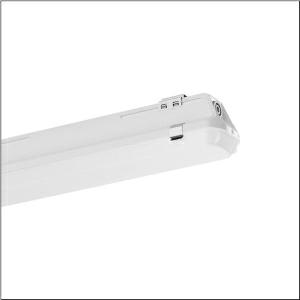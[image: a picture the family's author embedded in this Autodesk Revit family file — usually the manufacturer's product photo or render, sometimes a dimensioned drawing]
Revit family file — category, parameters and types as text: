
# Revit family: monsun_r__21_51fb10dl420j_0d51
name_source: partatom
category: Lighting Fixtures
units: mm (PartAtom-declared; Revit-internal decimal feet)

## family parameters
Cut with Voids When Loaded = No
Host = Face
Light Source = No
Part Type = Normal
Room Calculation Point = No
Round Connector Dimension = Use Diameter
Shared = No

## types (1)
- --- (1 x LED, 2630 lm, 16.6 W, 4000K)
    Apparent Load = 17 VA
    CIE Flux Codes = 46 76 93 94 100
    Color Rendering = 80
    Color Temperature = 4000K
    Default Elevation = 1800 mm
    Description = Monsun® 21, damp-proof luminaire, chain hanger, primary optical cover: enclosure, of PMMA, light emission: direct distribution, primary light characteristic: symmetric, installation type: suspended mounting, surface-mounted, horizontal mounting, vertical mounting, LED, rated luminous flux: 2.660lm, luminous efficacy: 155lm/W, light colour: 840, colour temperature: 4000K, control gear: ECG DALI, with terminal, 5-pole, max. 2.5mm², mains connection: 220..240V, AC, 50/60Hz, rated input power: 17W, housing, of glass-fibre reinforced plastic, uncoated, bright grey, incl. chain hanger, length: 1.299mm, width: 90mm, height: 88mm, clip for enclosure, of stainless steel (V2A), ceiling mounting element, of stainless steel (V2A), chain hanger, of stainless steel (V2A), protection rating (complete): IP66, insulation class (complete): insulation class I (protective earthing), certification: CE, ENEC, VDE, UKCA, protection symbol: D, impact resistance: IK04, permissible operating ambient temperature: -25..+35°C, standard: EN 50419, EN 60598-2-1, corresponds to IFS (International Featured Standards) requirements for safety and quality in the food industry, for indoor or canopied outdoor use, no direct snow, no direct sun, no direct rain, contact your sales advisor before using the luminaires in applications with unclear chemical exposure, large temperature fluctuations or condensation-forming humidity, LABS conformity tested according to VDMA 24364:2018-05, packaging unit: 1 piece
    Height = 88 mm
    Lamp = 1 x LED
    Lamp Light Flux = 2630 lm
    Lamp Power = 16.6 W
    Lamp count = 1
    Length = 1299 mm
    Luminous efficacy = 158 lm/W
    Manufacturer = Siteco
    ModVariant = No
    Model = 51FB10DL420J
    Mounting Place = Ceiling
    Mounting Type = Surface mounted
    Number of Poles = 1
    OnlyDefault = Yes
    Power Factor = 1
    Product Name = Monsun® 21
    Product group = damp-proof luminaire
    ProductGroupID = 300
    Protection Class = Protection class I
    Protection Degree = IP 66
    RLX_Detail_Level = 1
    RLX_Emergency_Light_Flux = 0 lm
    RLX_Emergency_Type = 0
    RLX_Emergency_Type_DB = No
    RlxData = <blob elided: 93601 chars, md5=ac2ac200>
    Socket = socket
    Standby Power = 0 W
    System Light Flux = 2630 lm
    System Power = 17 W
    Type Comments = factory setting: luminous flux: 100 % | dim-lin: 254 | 107 mA
    Type Image = l_1006717.jpg
    URL = http://relux.com
    VarID = @adj_078033
    Voltage = 0 V
    Weight = 0.00 kg
    Width = 90 mm

## geometry (parser evidence)
native form markers: Blend x4, Sweep x13
no freeform markers — native parametric forms only
